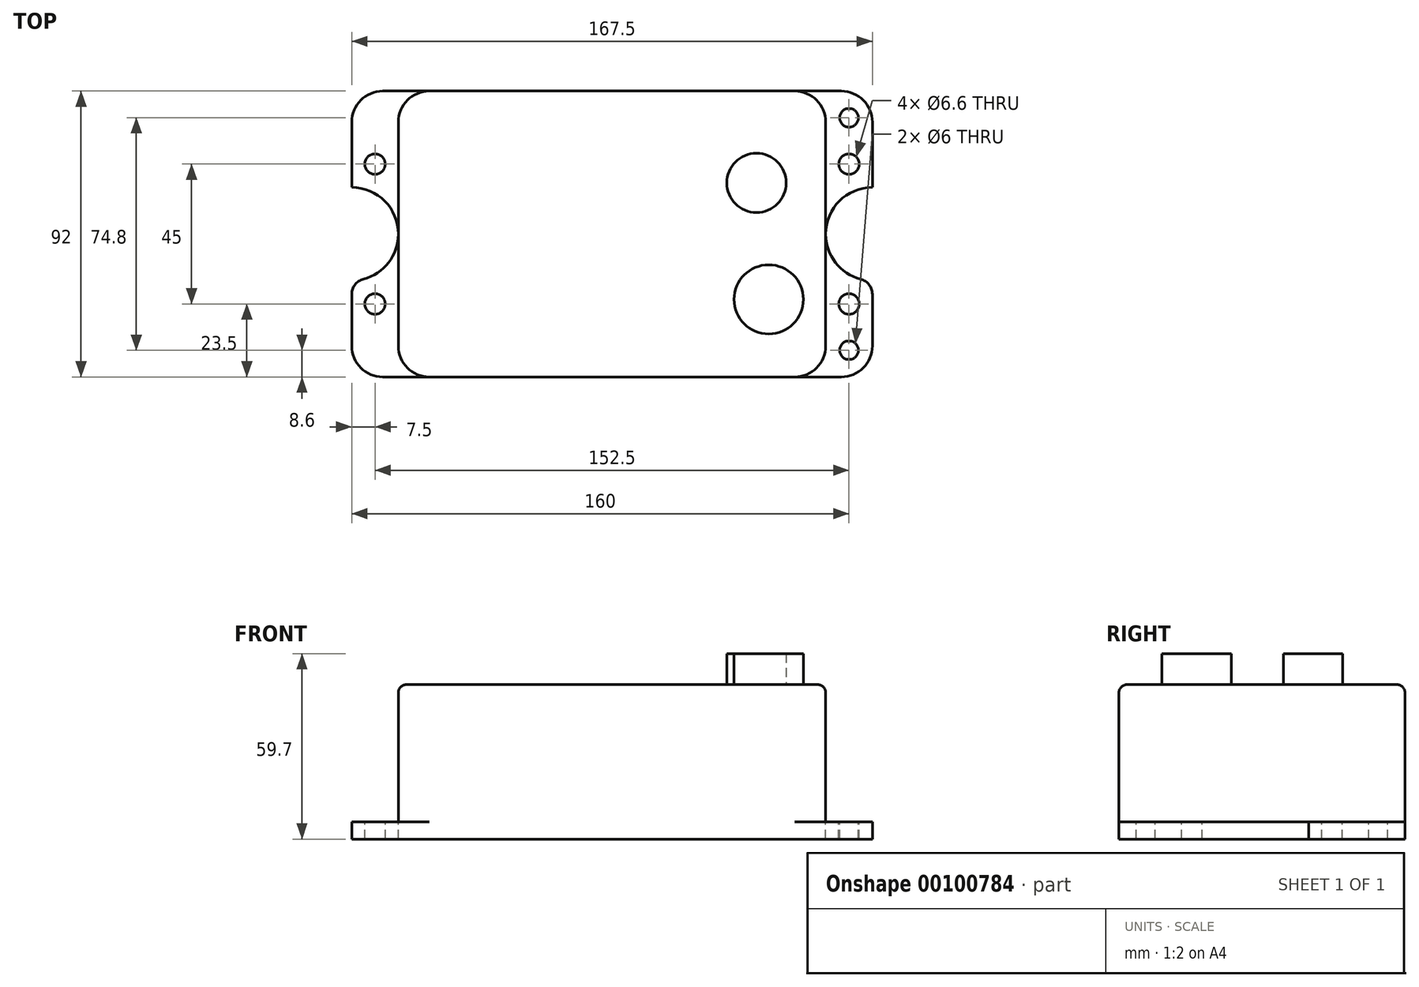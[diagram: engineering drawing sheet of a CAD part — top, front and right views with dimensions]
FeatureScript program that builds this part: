
annotation { "Feature Type Name" : "Feature", "Feature Type Description" : "" }
export const myFeature = defineFeature(function(context is Context, id is Id, definition is map)
    precondition{}
    {
        {
            var Q0;
            Q0=qCreatedBy(makeId("Top.planeOp"),FACE);
            var sketch = newSketch(context, id + "F0", { "sketchPlane" : qUnion([Q0])});
            skLineSegment(sketch, "E0.bottom", {"start": v(83.75, 46) * mm, "end": v(-83.75, 46) * mm});
            skLineSegment(sketch, "E0.top", {"start": v(83.75, -46) * mm, "end": v(-83.75, -46) * mm});
            skLineSegment(sketch, "E0.left", {"start": v(83.75, 46) * mm, "end": v(83.75, -46) * mm});
            skLineSegment(sketch, "E0.right", {"start": v(-83.75, 46) * mm, "end": v(-83.75, -46) * mm});
            skPoint(sketch, "E0.middle", {"position": v(0, 0) * mm});
            skSolve(sketch);
        }
        {
            var Q0;
            Q0 = qSketchRegion(id + "F0", true);
            extrude(context, id + "F1", {"entities" : qUnion([Q0]), "depth" : 5.5 * mm});
        }
        {
            var Q0;
            Q0=qCreatedBy(makeId("Top.planeOp"),FACE);
            var sketch = newSketch(context, id + "F2", { "sketchPlane" : qUnion([Q0])});
            skLineSegment(sketch, "E1.bottom", {"start": v(68.75, -46) * mm, "end": v(-68.75, -46) * mm});
            skLineSegment(sketch, "E1.top", {"start": v(68.75, 46) * mm, "end": v(-68.75, 46) * mm});
            skLineSegment(sketch, "E1.left", {"start": v(68.75, -46) * mm, "end": v(68.75, 46) * mm});
            skLineSegment(sketch, "E1.right", {"start": v(-68.75, -46) * mm, "end": v(-68.75, 46) * mm});
            skPoint(sketch, "E1.middle", {"position": v(0, 0) * mm});
            skSolve(sketch);
        }
        {
            var Q0;
            Q0 = qSketchRegion(id + "F2", true);
            extrude(context, id + "F3", {"entities" : qUnion([Q0]), "operationType" : NewBodyOperationType.ADD, "depth" : 49.7 * mm});
        }
        {
            var Q0;
            Q0=makeQuery(id+"F1.opExtrude","SWEPT_EDGE",EDGE,{"disambiguationData":[OSD([sQuery(id+"F0.wireOp",EDGE,"E0.top"),sQuery(id+"F0.wireOp",EDGE,"E0.right")])]});
            var Q1;
            Q1=makeQuery(id+"F1.opExtrude","SWEPT_EDGE",EDGE,{"disambiguationData":[OSD([sQuery(id+"F0.wireOp",EDGE,"E0.top"),sQuery(id+"F0.wireOp",EDGE,"E0.left")])]});
            var Q2;
            Q2=makeQuery(id+"F1.opExtrude","SWEPT_EDGE",EDGE,{"disambiguationData":[OSD([sQuery(id+"F0.wireOp",EDGE,"E0.bottom"),sQuery(id+"F0.wireOp",EDGE,"E0.left")])]});
            var Q3;
            Q3=makeQuery(id+"F1.opExtrude","SWEPT_EDGE",EDGE,{"disambiguationData":[OSD([sQuery(id+"F0.wireOp",EDGE,"E0.bottom"),sQuery(id+"F0.wireOp",EDGE,"E0.right")])]});
            var Q4;
            Q4=makeQuery(id+"F3.opExtrude","SWEPT_EDGE",EDGE,{"disambiguationData":[OSD([sQuery(id+"F2.wireOp",EDGE,"E1.top"),sQuery(id+"F2.wireOp",EDGE,"E1.right")])]});
            var Q5;
            Q5=makeQuery(id+"F3.opExtrude","SWEPT_EDGE",EDGE,{"disambiguationData":[OSD([sQuery(id+"F2.wireOp",EDGE,"E1.bottom"),sQuery(id+"F2.wireOp",EDGE,"E1.right")])]});
            var Q6;
            Q6=makeQuery(id+"F3.opExtrude","SWEPT_EDGE",EDGE,{"disambiguationData":[OSD([sQuery(id+"F2.wireOp",EDGE,"E1.top"),sQuery(id+"F2.wireOp",EDGE,"E1.left")])]});
            var Q7;
            Q7=makeQuery(id+"F3.opExtrude","SWEPT_EDGE",EDGE,{"disambiguationData":[OSD([sQuery(id+"F2.wireOp",EDGE,"E1.bottom"),sQuery(id+"F2.wireOp",EDGE,"E1.left")])]});
            fillet(context, id + "F4", {"entities" : qUnion([Q0, Q1, Q2, Q3, Q4, Q5, Q6, Q7]), "radius" : 10 * mm, "tangentPropagation" : true, "allowEdgeOverflow" : false});
        }
        {
            var Q0;
            Q0=makeQuery(id+"F3.opExtrude","CAP_EDGE",EDGE,{"disambiguationData":[OSD([sQuery(id+"F2.wireOp",EDGE,"E1.bottom")])],"isStart":false});
            fillet(context, id + "F5", {"entities" : qUnion([Q0]), "radius" : 2.54 * mm, "tangentPropagation" : true, "allowEdgeOverflow" : false});
        }
        {
            var Q0;
            {var subQ0=sQuery(id+"F0.wireOp",EDGE,"E0.left");var subQ1=sQuery(id+"F0.wireOp",EDGE,"E0.top");var subQ2=sQuery(id+"F0.wireOp",EDGE,"E0.bottom");Q0=makeQuery(id+"F3.boolean.opBoolean","SPLIT",FACE,{"disambiguationData":[TD([makeQuery(id+"F1.opExtrude","SWEPT_FACE",FACE,{"disambiguationData":[OSD([subQ0])]})])],"derivedFrom":makeQuery(id+"F1.opExtrude","CAP_FACE",FACE,{"disambiguationData":[OSD([subQ2,subQ1,subQ0,sQuery(id+"F0.wireOp",EDGE,"E0.right")])],"isStart":false})});}
            var sketch = newSketch(context, id + "F6", { "sketchPlane" : qUnion([Q0])});
            skCircle(sketch, "E2", {"center": v(-76.25, 22.5) * mm, "radius": 3.3 * mm});
            skCircle(sketch, "E3", {"center": v(-76.25, -22.5) * mm, "radius": 3.3 * mm});
            skCircle(sketch, "E4", {"center": v(76.25, -22.5) * mm, "radius": 3.3 * mm});
            skCircle(sketch, "E5", {"center": v(76.25, 22.5) * mm, "radius": 3.3 * mm});
            skCircle(sketch, "E6", {"center": v(76.25, 37.4) * mm, "radius": 3 * mm});
            skCircle(sketch, "E7", {"center": v(76.25, -37.4) * mm, "radius": 3 * mm});
            skSolve(sketch);
        }
        {
            var Q0;
            Q0=makeQuery(id+"F6.imprint","IMPRINT",FACE,{"disambiguationData":[TD([[makeQuery(id+"F6.imprint","IMPRINT",EDGE,{"derivedFrom":sQuery(id+"F6.wireOp",EDGE,"E2")}),1.0]])]});
            var Q1;
            Q1=makeQuery(id+"F6.imprint","IMPRINT",FACE,{"disambiguationData":[TD([[makeQuery(id+"F6.imprint","IMPRINT",EDGE,{"derivedFrom":sQuery(id+"F6.wireOp",EDGE,"E3")}),1.0]])]});
            var Q2;
            Q2=makeQuery(id+"F6.imprint","IMPRINT",FACE,{"disambiguationData":[TD([[makeQuery(id+"F6.imprint","IMPRINT",EDGE,{"derivedFrom":sQuery(id+"F6.wireOp",EDGE,"E5")}),1.0]])]});
            var Q3;
            {var subQ0=sQuery(id+"F6.wireOp",EDGE,"E4");var subQ1=makeQuery(id+"F3.boolean.opBoolean","INTERSECT",EDGE,{"derivedFrom":[makeQuery(id+"F1.opExtrude","CAP_FACE",FACE,{"disambiguationData":[OSD([sQuery(id+"F0.wireOp",EDGE,"E0.bottom"),sQuery(id+"F0.wireOp",EDGE,"E0.top"),sQuery(id+"F0.wireOp",EDGE,"E0.left"),sQuery(id+"F0.wireOp",EDGE,"E0.right")])],"isStart":false}),makeQuery(id+"F3.opExtrude","SWEPT_FACE",FACE,{"disambiguationData":[OSD([sQuery(id+"F2.wireOp",EDGE,"E1.left")])]})]});var subQ2=makeQuery(id+"F6.imprint","INTERSECT",VERTEX,{"disambiguationData":[OD(0.0)],"derivedFrom":[subQ1,subQ0]});Q3=makeQuery(id+"F6.imprint","IMPRINT",FACE,{"disambiguationData":[TD([[makeQuery(id+"F6.imprint","IMPRINT",EDGE,{"disambiguationData":[TD([[subQ2,-1.0]])],"derivedFrom":subQ0}),1.0]])]});}
            var Q4;
            Q4=makeQuery(id+"F6.imprint","IMPRINT",FACE,{"disambiguationData":[TD([[makeQuery(id+"F6.imprint","IMPRINT",EDGE,{"derivedFrom":sQuery(id+"F6.wireOp",EDGE,"E7")}),1.0]])]});
            var Q5;
            Q5=makeQuery(id+"F6.imprint","IMPRINT",FACE,{"disambiguationData":[TD([[makeQuery(id+"F6.imprint","IMPRINT",EDGE,{"derivedFrom":sQuery(id+"F6.wireOp",EDGE,"E6")}),1.0]])]});
            extrude(context, id + "F7", {"entities" : qUnion([Q0, Q1, Q2, Q3, Q4, Q5]), "operationType" : NewBodyOperationType.REMOVE, "oppositeDirection" : true, "depth" : 5.5 * mm});
        }
        {
            var Q0;
            {var subQ0=sQuery(id+"F0.wireOp",EDGE,"E0.right");var subQ1=sQuery(id+"F0.wireOp",EDGE,"E0.top");var subQ2=sQuery(id+"F0.wireOp",EDGE,"E0.bottom");Q0=makeQuery(id+"F3.boolean.opBoolean","SPLIT",FACE,{"disambiguationData":[TD([makeQuery(id+"F1.opExtrude","SWEPT_FACE",FACE,{"disambiguationData":[OSD([subQ0])]})])],"derivedFrom":makeQuery(id+"F1.opExtrude","CAP_FACE",FACE,{"disambiguationData":[OSD([subQ2,subQ1,sQuery(id+"F0.wireOp",EDGE,"E0.left"),subQ0])],"isStart":false})});}
            var sketch = newSketch(context, id + "F8", { "sketchPlane" : qUnion([Q0])});
            skCircle(sketch, "E8", {"center": v(-83.75, 0) * mm, "radius": 15 * mm});
            skSolve(sketch);
        }
        {
            var Q0;
            {var subQ0=sQuery(id+"F0.wireOp",EDGE,"E0.left");var subQ1=sQuery(id+"F0.wireOp",EDGE,"E0.top");var subQ2=sQuery(id+"F0.wireOp",EDGE,"E0.bottom");Q0=makeQuery(id+"F3.boolean.opBoolean","SPLIT",FACE,{"disambiguationData":[TD([makeQuery(id+"F1.opExtrude","SWEPT_FACE",FACE,{"disambiguationData":[OSD([subQ0])]})])],"derivedFrom":makeQuery(id+"F1.opExtrude","CAP_FACE",FACE,{"disambiguationData":[OSD([subQ2,subQ1,subQ0,sQuery(id+"F0.wireOp",EDGE,"E0.right")])],"isStart":false})});}
            var sketch = newSketch(context, id + "F9", { "sketchPlane" : qUnion([Q0])});
            skCircle(sketch, "E9", {"center": v(83.75, 0) * mm, "radius": 15 * mm});
            skSolve(sketch);
        }
        {
            var Q0;
            {var subQ0=sQuery(id+"F8.wireOp",EDGE,"E8");var subQ1=sQuery(id+"F0.wireOp",EDGE,"E0.right");var subQ2=makeQuery(id+"F1.opExtrude","CAP_EDGE",EDGE,{"disambiguationData":[OSD([subQ1])],"isStart":false});var subQ3=makeQuery(id+"F8.imprint","INTERSECT",VERTEX,{"disambiguationData":[OD(0.0)],"derivedFrom":[subQ2,subQ0]});Q0=makeQuery(id+"F8.imprint","IMPRINT",FACE,{"disambiguationData":[TD([[makeQuery(id+"F8.imprint","IMPRINT",EDGE,{"disambiguationData":[TD([[subQ3,-1.0]])],"derivedFrom":subQ2}),1.0]])]});}
            var Q1;
            {var subQ0=sQuery(id+"F9.wireOp",EDGE,"E9");var subQ4=sQuery(id+"F0.wireOp",EDGE,"E0.left");var subQ9=makeQuery(id+"F1.opExtrude","CAP_EDGE",EDGE,{"disambiguationData":[OSD([subQ4])],"isStart":false});var subQ10=makeQuery(id+"F9.imprint","INTERSECT",VERTEX,{"disambiguationData":[OD(0.0)],"derivedFrom":[subQ9,subQ0]});Q1=makeQuery(id+"F9.imprint","IMPRINT",FACE,{"disambiguationData":[TD([[makeQuery(id+"F9.imprint","IMPRINT",EDGE,{"disambiguationData":[TD([[subQ10,-1.0]])],"derivedFrom":subQ9}),-1.0]])]});}
            extrude(context, id + "F10", {"entities" : qUnion([Q0, Q1]), "operationType" : NewBodyOperationType.REMOVE, "oppositeDirection" : true, "depth" : 5.5 * mm});
        }
        {
            var Q0;
            {var subQ0=sQuery(id+"F9.wireOp",EDGE,"E9");var subQ1=sQuery(id+"F0.wireOp",EDGE,"E0.left");Q0=makeQuery(id+"F10.boolean.opBoolean","COPY",EDGE,{"derivedFrom":makeQuery(id+"F10.opExtrude","SWEPT_EDGE",EDGE,{"disambiguationData":[OSD([subQ1,subQ0]),TDD([makeQuery(id+"F9.imprint","INTERSECT",VERTEX,{"disambiguationData":[OD(1.0)],"derivedFrom":[makeQuery(id+"F1.opExtrude","CAP_EDGE",EDGE,{"disambiguationData":[OSD([subQ1])],"isStart":false}),subQ0]})])]})});}
            var Q1;
            {var subQ0=sQuery(id+"F8.wireOp",EDGE,"E8");var subQ1=sQuery(id+"F0.wireOp",EDGE,"E0.right");Q1=makeQuery(id+"F10.boolean.opBoolean","COPY",EDGE,{"derivedFrom":makeQuery(id+"F10.opExtrude","SWEPT_EDGE",EDGE,{"disambiguationData":[OSD([subQ1,subQ0]),TDD([makeQuery(id+"F8.imprint","INTERSECT",VERTEX,{"disambiguationData":[OD(1.0)],"derivedFrom":[makeQuery(id+"F1.opExtrude","CAP_EDGE",EDGE,{"disambiguationData":[OSD([subQ1])],"isStart":false}),subQ0]})])]})});}
            var Q2;
            {var subQ0=sQuery(id+"F8.wireOp",EDGE,"E8");var subQ1=sQuery(id+"F0.wireOp",EDGE,"E0.right");Q2=makeQuery(id+"F10.boolean.opBoolean","COPY",EDGE,{"derivedFrom":makeQuery(id+"F10.opExtrude","SWEPT_EDGE",EDGE,{"disambiguationData":[OSD([subQ1,subQ0]),TDD([makeQuery(id+"F8.imprint","INTERSECT",VERTEX,{"disambiguationData":[OD(0.0)],"derivedFrom":[makeQuery(id+"F1.opExtrude","CAP_EDGE",EDGE,{"disambiguationData":[OSD([subQ1])],"isStart":false}),subQ0]})])]})});}
            var Q3;
            {var subQ0=sQuery(id+"F9.wireOp",EDGE,"E9");var subQ1=sQuery(id+"F0.wireOp",EDGE,"E0.left");Q3=makeQuery(id+"F10.boolean.opBoolean","COPY",EDGE,{"derivedFrom":makeQuery(id+"F10.opExtrude","SWEPT_EDGE",EDGE,{"disambiguationData":[OSD([subQ1,subQ0]),TDD([makeQuery(id+"F9.imprint","INTERSECT",VERTEX,{"disambiguationData":[OD(0.0)],"derivedFrom":[makeQuery(id+"F1.opExtrude","CAP_EDGE",EDGE,{"disambiguationData":[OSD([subQ1])],"isStart":false}),subQ0]})])]})});}
            fillet(context, id + "F11", {"entities" : qUnion([Q0, Q1, Q2, Q3]), "radius" : 5 * mm, "tangentPropagation" : true, "allowEdgeOverflow" : false});
        }
        {
            var Q0;
            Q0=makeQuery(id+"F3.opExtrude","CAP_FACE",FACE,{"disambiguationData":[OSD([sQuery(id+"F2.wireOp",EDGE,"E1.bottom"),sQuery(id+"F2.wireOp",EDGE,"E1.top"),sQuery(id+"F2.wireOp",EDGE,"E1.left"),sQuery(id+"F2.wireOp",EDGE,"E1.right")])],"isStart":false});
            var sketch = newSketch(context, id + "F12", { "sketchPlane" : qUnion([Q0])});
            skCircle(sketch, "E10", {"center": v(46.47, 16.46) * mm, "radius": 9.54 * mm});
            skCircle(sketch, "E11", {"center": v(50.43, -21.05) * mm, "radius": 11.13 * mm});
            skSolve(sketch);
        }
        {
            var Q0;
            Q0=makeQuery(id+"F12.imprint","IMPRINT",FACE,{"disambiguationData":[TD([[makeQuery(id+"F12.imprint","IMPRINT",EDGE,{"derivedFrom":sQuery(id+"F12.wireOp",EDGE,"E11")}),1.0]])]});
            var Q1;
            Q1=makeQuery(id+"F12.imprint","IMPRINT",FACE,{"disambiguationData":[TD([[makeQuery(id+"F12.imprint","IMPRINT",EDGE,{"derivedFrom":sQuery(id+"F12.wireOp",EDGE,"E10")}),1.0]])]});
            extrude(context, id + "F13", {"entities" : qUnion([Q0, Q1]), "operationType" : NewBodyOperationType.ADD, "depth" : 10 * mm});
        }
    });
